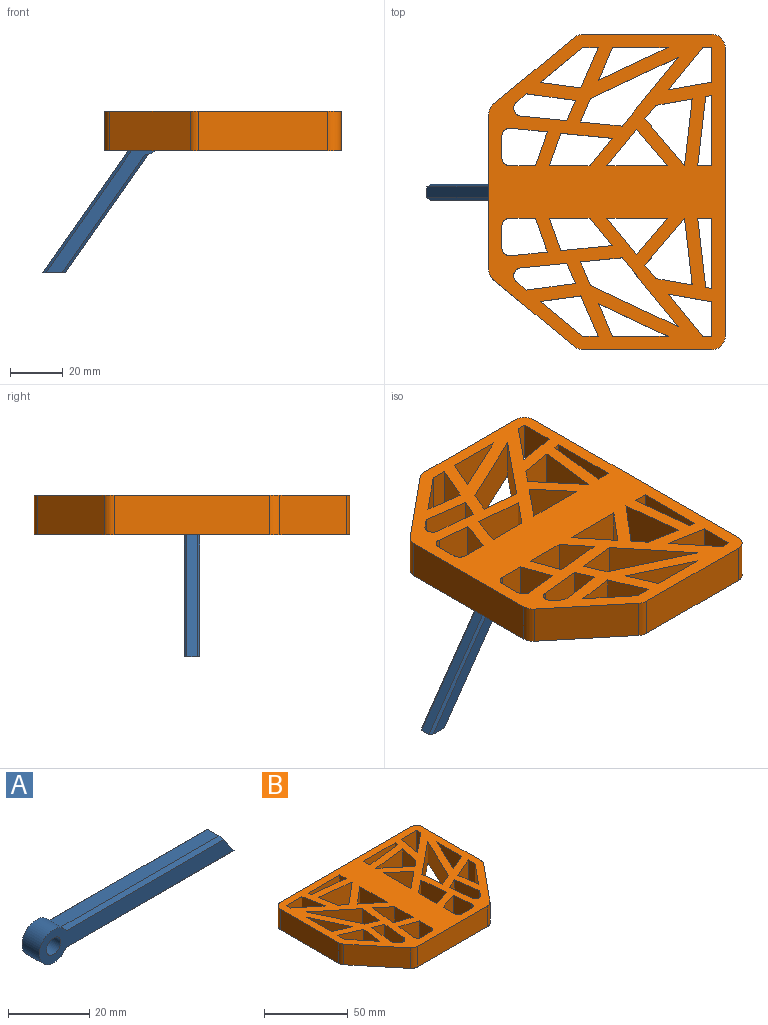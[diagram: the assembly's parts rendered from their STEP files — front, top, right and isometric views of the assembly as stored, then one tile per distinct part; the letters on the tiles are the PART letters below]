
ASSEMBLY  parts=2 mates=1
PART A: 11 faces, bbox 68.6x6x10 mm
  f0: plane 60x4mm, normal (0,0,-1), area 240mm2, adj f1,f3,f7,f8
  f1: plane 7x6mm, normal (0.81,0,0.58), area 49.2mm2, adj f0,f2,f5,f6,f7,f8,f9,f10
  f2: plane 55x4mm, normal (0,0,1), area 220mm2, adj f1,f3,f9,f10
  f3: cylinder r=5mm len=10mm, axis (0,1,0), area 144.6mm2, adj f0,f2,f5,f6,f7,f8,f9,f10
  f4: cylinder r=2.5mm len=6mm, axis (0,1,0), area 94.2mm2, adj f5,f6
  f5: plane 67.86x10mm, normal (0,-1,0), area 340.3mm2, adj f1,f3,f4,f7,f9
  f6: plane 67.86x10mm, normal (0,1,0), area 340.3mm2, adj f1,f3,f4,f8,f10
  f7: plane 60x1mm, normal (0,-0.71,-0.71), area 83.8mm2, adj f0,f1,f3,f5
  f8: plane 60x1mm, normal (0,0.71,-0.71), area 83.8mm2, adj f0,f1,f3,f6
  f9: plane 55.71x1mm, normal (0,-0.71,0.71), area 77.7mm2, adj f1,f2,f3,f5
  f10: plane 55.71x1mm, normal (0,0.71,0.71), area 77.7mm2, adj f1,f2,f3,f6
PART B: 104 faces, bbox 120x90x15 mm
  f0: plane 120x90mm, normal (0,0,-1), area 5493mm2, adj f1,f2,f3,f4,f5,f6,f7,f8
  f1: plane 15.86x15mm, normal (1,0.1,0), area 239.1mm2, adj f0,f2,f84,f85
  f2: plane 26.23x21.31mm, normal (0.63,-0.78,0), area 506.9mm2, adj f0,f1,f3,f85
  f3: plane 33.3x15.69mm, normal (-0.9,0.43,0), area 552.2mm2, adj f0,f2,f84,f85
  f4: plane 15.46x15mm, normal (1,0,0), area 232mm2, adj f0,f5,f64,f85
  f5: plane 15x10.4mm, normal (0.63,-0.78,0), area 201mm2, adj f0,f4,f6,f85
  f6: plane 19.57x15mm, normal (-1,-0.1,0), area 295mm2, adj f0,f5,f64,f85
  f7: plane 23x15mm, normal (1,0,0), area 345mm2, adj f0,f8,f65,f85
  f8: plane 15x13.89mm, normal (-0.64,-0.76,0), area 272.5mm2, adj f0,f7,f65,f85
  f9: plane 17.84x15.05mm, normal (0.64,0.76,0), area 350.1mm2, adj f0,f10,f66,f85
  f10: plane 25.41x15mm, normal (0.11,-0.99,0), area 383.7mm2, adj f0,f9,f11,f85
  f11: plane 15x13.8mm, normal (-0.98,0.17,0), area 210.2mm2, adj f0,f10,f66,f85
  f12: plane 17.84x15.05mm, normal (-0.64,0.76,0), area 350.1mm2, adj f0,f13,f67,f85
  f13: plane 15x5.14mm, normal (0.63,0.78,0), area 99.3mm2, adj f0,f12,f14,f85
  f14: plane 15x13.8mm, normal (0.98,0.17,0), area 210.2mm2, adj f0,f13,f67,f85
  f15: plane 15x13.89mm, normal (0.63,0.78,0), area 268.4mm2, adj f0,f16,f68,f85
  f16: plane 15x13.89mm, normal (0.64,-0.76,0), area 272.5mm2, adj f0,f15,f68,f85
  f17: plane 15x12.36mm, normal (0.33,0.94,0), area 196.6mm2, adj f0,f18,f69,f85
  f18: plane 19.57x15mm, normal (1,-0.1,0), area 295mm2, adj f0,f17,f19,f85
  f19: plane 15x10.4mm, normal (-0.63,-0.78,0), area 201mm2, adj f0,f18,f69,f85
  f20: plane 15.4x15mm, normal (0.4,-0.92,0), area 251.6mm2, adj f0,f21,f70,f85
  f21: plane 15x5.93mm, normal (-1,0,0), area 89mm2, adj f0,f20,f22,f85
  f22: plane 16.16x15mm, normal (-0.77,0.64,0), area 314mm2, adj f0,f21,f70,f85
  f23: plane 26.49x15mm, normal (0.9,-0.43,0), area 439.2mm2, adj f0,f24,f71,f85
  f24: plane 21.1x15mm, normal (-1,0,0), area 316.5mm2, adj f0,f23,f71,f85
  f25: plane 16.52x15mm, normal (0.98,-0.17,0), area 251.6mm2, adj f0,f26,f72,f85
  f26: plane 15x13.18mm, normal (0,-1,0), area 197.7mm2, adj f0,f25,f27,f85
  f27: plane 15x3.44mm, normal (-1,0,0), area 51.6mm2, adj f0,f26,f72,f85
  f28: plane 16.1x15mm, normal (0.63,0.78,0), area 311.1mm2, adj f0,f29,f73,f85
  f29: plane 15x3.44mm, normal (1,0,0), area 51.6mm2, adj f0,f28,f30,f85
  f30: plane 15x13.18mm, normal (0,-1,0), area 197.7mm2, adj f0,f29,f73,f85
  f31: plane 15x3.81mm, normal (-0.77,0.64,0), area 74mm2, adj f0,f74,f85,f101
  f32: plane 17.53x15mm, normal (1,0.1,0), area 264.3mm2, adj f0,f33,f85,f101
  f33: plane 15x7.67mm, normal (0.4,-0.92,0), area 125.3mm2, adj f0,f32,f74,f85
  f34: plane 15x9.79mm, normal (-1,0,0), area 146.9mm2, adj f0,f75,f85,f99
  f35: plane 15x8.3mm, normal (0,1,0), area 124.5mm2, adj f0,f85,f99,f100
  f36: plane 15x14.02mm, normal (1,-0.1,0), area 211.3mm2, adj f0,f75,f85,f100
  f37: plane 15x8.3mm, normal (0,1,0), area 124.5mm2, adj f0,f85,f98,f102
  f38: plane 15x9.79mm, normal (1,0,0), area 146.9mm2, adj f0,f39,f85,f98
  f39: plane 15x12.88mm, normal (0.33,-0.94,0), area 204.7mm2, adj f0,f38,f76,f85
  f40: plane 26.75x15mm, normal (0,-1,0), area 401.2mm2, adj f0,f41,f77,f85
  f41: plane 15x5.42mm, normal (-1,0,0), area 81.4mm2, adj f0,f40,f42,f85
  f42: plane 26.32x15mm, normal (0.11,0.99,0), area 397.4mm2, adj f0,f41,f77,f85
  f43: plane 15x5.42mm, normal (1,0,0), area 81.4mm2, adj f0,f44,f78,f85
  f44: plane 26.75x15mm, normal (0,-1,0), area 401.2mm2, adj f0,f43,f45,f85
  f45: plane 15x2.4mm, normal (-0.98,0.17,0), area 36.5mm2, adj f0,f44,f78,f85
  f46: plane 49.21x15mm, normal (-1,0,0), area 738.1mm2, adj f0,f79,f85,f91
  f47: plane 30.79x25.36mm, normal (-0.77,-0.64,0), area 598.4mm2, adj f0,f85,f89,f91
  f48: plane 59.28x15mm, normal (0,-1,0), area 889.2mm2, adj f0,f85,f89,f90
  f49: plane 30.79x25.36mm, normal (0.77,-0.64,0), area 598.4mm2, adj f0,f85,f90,f92
  f50: plane 49.21x15mm, normal (1,0,0), area 738.1mm2, adj f0,f51,f85,f92
  f51: cylinder r=5mm len=15mm, axis (0,0,-1), area 117.8mm2, adj f0,f50,f52,f85
  f52: plane 110x15mm, normal (0,1,0), area 1650mm2, adj f0,f51,f79,f85
  f53: plane 15.86x15mm, normal (-1,0.1,0), area 239.1mm2, adj f0,f54,f80,f85
  f54: plane 15x8.95mm, normal (0.4,0.92,0), area 146.2mm2, adj f0,f53,f55,f85
  f55: plane 33.3x15.69mm, normal (0.9,0.43,0), area 552.2mm2, adj f0,f54,f80,f85
  f56: plane 15x12.48mm, normal (0.4,0.92,0), area 203.8mm2, adj f0,f57,f81,f85
  f57: plane 21.1x15mm, normal (1,0,0), area 316.5mm2, adj f0,f56,f81,f85
  f58: plane 18.65x15mm, normal (0.99,-0.13,0), area 282.2mm2, adj f0,f59,f82,f85
  f59: plane 15x7.67mm, normal (-0.4,-0.92,0), area 125.3mm2, adj f0,f58,f60,f85
  f60: plane 17.53x15mm, normal (-1,0.1,0), area 264.3mm2, adj f0,f59,f85,f97
  f61: plane 15x5.93mm, normal (1,0,0), area 89mm2, adj f0,f62,f83,f85
  f62: plane 15.4x15mm, normal (-0.4,-0.92,0), area 251.6mm2, adj f0,f61,f63,f85
  f63: plane 15.44x15mm, normal (-0.99,0.13,0), area 233.8mm2, adj f0,f62,f83,f85
  f64: plane 15x12.36mm, normal (-0.33,0.94,0), area 196.6mm2, adj f0,f4,f6,f85
  f65: plane 15x13.89mm, normal (-0.63,0.78,0), area 268.4mm2, adj f0,f7,f8,f85
  f66: plane 15x5.14mm, normal (-0.63,0.78,0), area 99.3mm2, adj f0,f9,f11,f85
  f67: plane 25.41x15mm, normal (-0.11,-0.99,0), area 383.7mm2, adj f0,f12,f14,f85
  f68: plane 23x15mm, normal (-1,0,0), area 345mm2, adj f0,f15,f16,f85
  f69: plane 15.46x15mm, normal (-1,0,0), area 232mm2, adj f0,f17,f19,f85
  f70: plane 15.44x15mm, normal (0.99,0.13,0), area 233.8mm2, adj f0,f20,f22,f85
  f71: plane 15x12.48mm, normal (-0.4,0.92,0), area 203.8mm2, adj f0,f23,f24,f85
  f72: plane 16.1x15mm, normal (-0.63,0.78,0), area 311.1mm2, adj f0,f25,f27,f85
  f73: plane 16.52x15mm, normal (-0.98,-0.17,0), area 251.6mm2, adj f0,f28,f30,f85
  f74: plane 18.65x15mm, normal (-0.99,-0.13,0), area 282.2mm2, adj f0,f31,f33,f85
  f75: plane 15x12.88mm, normal (-0.33,-0.94,0), area 204.7mm2, adj f0,f34,f36,f85
  f76: plane 15x14.02mm, normal (-1,-0.1,0), area 211.3mm2, adj f0,f39,f85,f102
  f77: plane 15x2.4mm, normal (0.98,0.17,0), area 36.5mm2, adj f0,f40,f42,f85
  f78: plane 26.32x15mm, normal (-0.11,0.99,0), area 397.4mm2, adj f0,f43,f45,f85
  f79: cylinder r=5mm len=15mm, axis (0,0,-1), area 117.8mm2, adj f0,f46,f52,f85
  f80: plane 26.23x21.31mm, normal (-0.63,-0.78,0), area 506.9mm2, adj f0,f53,f55,f85
  f81: plane 26.49x15mm, normal (-0.9,-0.43,0), area 439.2mm2, adj f0,f56,f57,f85
  f82: plane 15x3.81mm, normal (0.77,0.64,0), area 74mm2, adj f0,f58,f85,f97
  f83: plane 16.16x15mm, normal (0.77,0.64,0), area 314mm2, adj f0,f61,f63,f85
  f84: plane 15x8.95mm, normal (-0.4,0.92,0), area 146.2mm2, adj f0,f1,f3,f85
  f85: plane 120x90mm, normal (0,0,1), area 6095.6mm2, adj f1,f2,f3,f4,f5,f6,f7,f8
  f86: plane 68x10mm, normal (-1,0,0), area 660.4mm2, adj f0,f88,f94,f96,f103
  f87: plane 68x10mm, normal (1,0,0), area 660.4mm2, adj f0,f88,f93,f95,f103
  f88: plane 77.8x8mm, normal (0,0,-1), area 602.7mm2, adj f86,f87,f93,f94,f95,f96
  f89: cylinder r=5mm len=15mm, axis (0,0,-1), area 66.1mm2, adj f0,f47,f48,f85
  f90: cylinder r=5mm len=15mm, axis (0,0,1), area 66.1mm2, adj f0,f48,f49,f85
  f91: cylinder r=5mm len=15mm, axis (0,0,-1), area 51.7mm2, adj f0,f46,f47,f85
  f92: cylinder r=5mm len=15mm, axis (0,0,-1), area 51.7mm2, adj f0,f49,f50,f85
  f93: cylinder r=5mm len=10mm, axis (0,0,1), area 68.5mm2, adj f0,f87,f88,f94
  f94: cylinder r=5mm len=10mm, axis (0,0,-1), area 68.5mm2, adj f0,f86,f88,f93
  f95: cylinder r=5mm len=10mm, axis (0,0,-1), area 68.5mm2, adj f0,f87,f88,f96
  f96: cylinder r=5mm len=10mm, axis (0,0,1), area 68.5mm2, adj f0,f86,f88,f95
  f97: cylinder r=3mm len=15mm, axis (0,0,-1), area 105.9mm2, adj f0,f60,f82,f85
  f98: cylinder r=3mm len=15mm, axis (0,0,1), area 70.7mm2, adj f0,f37,f38,f85
  f99: cylinder r=3mm len=15mm, axis (0,0,-1), area 70.7mm2, adj f0,f34,f35,f85
  f100: cylinder r=3mm len=15mm, axis (0,0,1), area 75.2mm2, adj f0,f35,f36,f85
  f101: cylinder r=3mm len=15mm, axis (0,0,1), area 105.9mm2, adj f0,f31,f32,f85
  f102: cylinder r=3mm len=15mm, axis (0,0,-1), area 75.2mm2, adj f0,f37,f76,f85
  f103: cylinder r=2.5mm len=8mm, axis (1,0,0), area 125.7mm2, adj f86,f87
PLACE A rot(axis=(0,1,0),125deg) t=(126.82,37.83,52.65)mm
PLACE B rot(axis=(0,0,-1),90deg) t=(156.05,34.83,49.15)mm
MATE revolute A.f4 <-> B.f103  axis (0,1,0) through (126.82,34.83,52.65)mm
